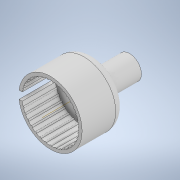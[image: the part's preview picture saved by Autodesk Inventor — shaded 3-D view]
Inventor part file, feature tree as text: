
AUTODESK INVENTOR PART (.ipt)
format: ipt  version: 2020 (Build 240168000, 168)  size: 278,016 bytes
history: native  units: in
note: dims shown in document units (in); Inventor stores cm internally (conversion verified against a paired STEP export)
features: extrude x9, sketch x9, fillet x1, other x1, pattern_circular x1
ambient origin geometry x8: Origin, YZ Plane, XZ Plane, XY Plane, X Axis, Y Axis, Z Axis, Center Point
bodies: Solid1 (feature_tree)
feature tree (21):
  extrude  "Extrusion1"  Depth=1.0in TaperAngle=0.0deg
  extrude  "Extrusion2"  Depth=0.42in TaperAngle=0.0deg
  extrude  "Extrusion3"  Depth=0.19in
  extrude  "Extrusion4"  Depth=0.45in
  fillet  "Fillet2"  Radius=0.45in
  extrude  "Extrusion5"  Depth=0.05in
  extrude  "Extrusion6"  Depth=0.45in TaperAngle=0.0deg
  sketch  "Sketch7"  dims[d19=0.1in d20=0.2in]
  other  "Work Axis1"
  extrude  "Extrusion7"  Depth=0.2in
  pattern_circular  "Circular Pattern1"  [2 undecoded]
  extrude  "Extrusion8"  Depth=0.42in TaperAngle=0.0deg
  extrude  "Extrusion9"  Depth=0.42in TaperAngle=360.0deg
  sketch  "Sketch1"  dims[d0=0.8in d1=1.0in d2=0.0in]
  sketch  "Sketch2"  dims[d3=0.72in d4=0.42in d5=0.0in]
  sketch  "Sketch3"  dims[d6=0.21in d7=0.19in]
  sketch  "Sketch4"  dims[d8=0.45in d9=-0.0069in d10=0.3in d11=0.45in d12=0.0in]
  sketch  "Sketch5"  dims[d14=0.125in d15=0.05in]
  sketch  "Sketch6"  dims[d16=0.1in d17=0.45in d18=0.0in]
  sketch  "Sketch8"  dims[d21=0.05in]
  sketch  "Sketch9"  dims[d22=0.42in d23=0.0in d24=0.02in d25=0.42in d26=0.0in d27=13.7795in d28=360.0deg d30=0.42in d31=0.0in d32=0.42in d33=0.0in]
note: 2 required parameter values undecoded (feature->parameter linkage not recoverable at this tier; creation-order binding heuristic only, values carry confidence <= 0.55)
